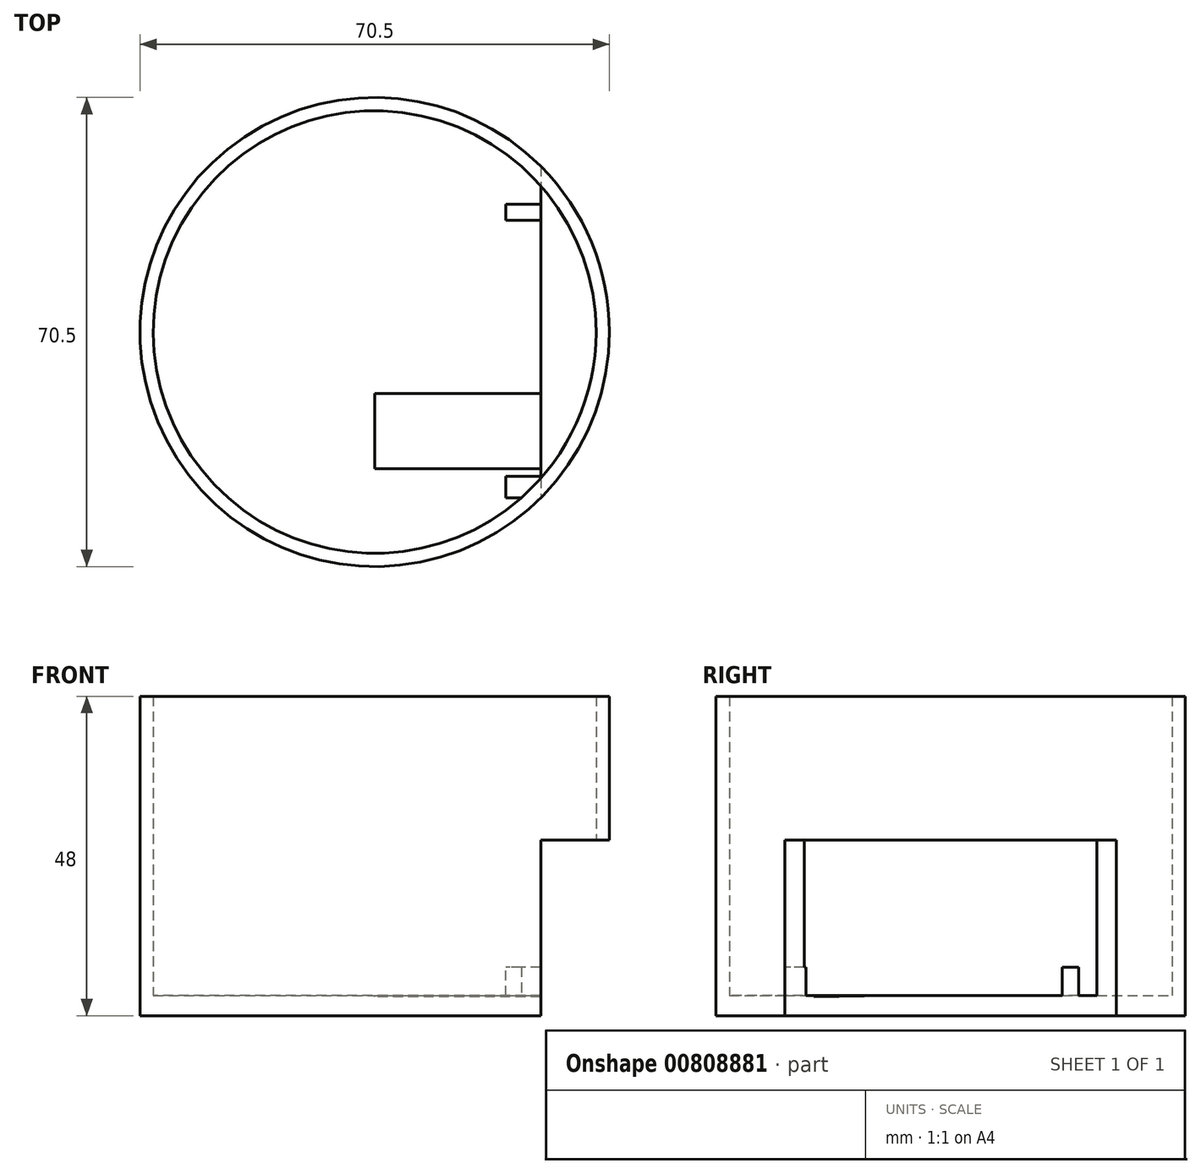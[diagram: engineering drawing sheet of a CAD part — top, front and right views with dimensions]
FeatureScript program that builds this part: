
annotation { "Feature Type Name" : "Feature", "Feature Type Description" : "" }
export const myFeature = defineFeature(function(context is Context, id is Id, definition is map)
    precondition{}
    {
        {
            var Q0;
            Q0=qCreatedBy(makeId("Top.planeOp"),FACE);
            var sketch = newSketch(context, id + "F0", { "sketchPlane" : qUnion([Q0])});
            skCircle(sketch, "E0", {"center": v(0, 0) * mm, "radius": 35.25 * mm});
            skSolve(sketch);
        }
        {
            var Q0;
            Q0=makeQuery(id+"F0.imprint","IMPRINT",FACE,{"disambiguationData":[TD([[makeQuery(id+"F0.imprint","IMPRINT",EDGE,{"derivedFrom":sQuery(id+"F0.wireOp",EDGE,"E0")}),1.0]])]});
            extrude(context, id + "F1", {"entities" : qUnion([Q0]), "depth" : 3 * mm, "offsetDistance" : 25 * mm});
        }
        {
            var Q0;
            Q0=makeQuery(id+"F1.opExtrude","CAP_FACE",FACE,{"disambiguationData":[OSD([sQuery(id+"F0.wireOp",EDGE,"E0")])],"isStart":false});
            var sketch = newSketch(context, id + "F2", { "sketchPlane" : qUnion([Q0])});
            skCircle(sketch, "E1", {"center": v(0, 0) * mm, "radius": 35.25 * mm});
            skCircle(sketch, "E2", {"center": v(0, 0) * mm, "radius": 33.25 * mm});
            skSolve(sketch);
        }
        {
            var Q0;
            Q0=makeQuery(id+"F2.imprint","IMPRINT",FACE,{"disambiguationData":[TD([[makeQuery(id+"F2.imprint","IMPRINT",EDGE,{"derivedFrom":sQuery(id+"F2.wireOp",EDGE,"E1")}),1.0]])]});
            extrude(context, id + "F3", {"entities" : qUnion([Q0]), "operationType" : NewBodyOperationType.ADD, "depth" : 45 * mm, "offsetDistance" : 25 * mm});
        }
        {
            var Q0;
            Q0=qCreatedBy(makeId("Right.planeOp"),FACE);
            var sketch = newSketch(context, id + "F4", { "sketchPlane" : qUnion([Q0])});
            skLineSegment(sketch, "E3.bottom", {"start": v(19.22, 0) * mm, "end": v(-24.9, 0) * mm});
            skLineSegment(sketch, "E3.top", {"start": v(19.22, 26.4) * mm, "end": v(-24.9, 26.4) * mm});
            skLineSegment(sketch, "E3.left", {"start": v(19.22, 0) * mm, "end": v(19.22, 26.4) * mm});
            skLineSegment(sketch, "E3.right", {"start": v(-24.9, 0) * mm, "end": v(-24.9, 26.4) * mm});
            skLineSegment(sketch, "E4.bottom", {"start": v(-21.71, 22.96) * mm, "end": v(16.77, 22.96) * mm});
            skLineSegment(sketch, "E4.top", {"start": v(-21.71, 2.61) * mm, "end": v(16.77, 2.61) * mm});
            skLineSegment(sketch, "E4.left", {"start": v(-21.71, 22.96) * mm, "end": v(-21.71, 2.61) * mm});
            skLineSegment(sketch, "E4.right", {"start": v(16.77, 22.96) * mm, "end": v(16.77, 2.61) * mm});
            skSolve(sketch);
        }
        {
            var Q0;
            Q0=makeQuery(id+"F4.imprint","IMPRINT",FACE,{"disambiguationData":[TD([[makeQuery(id+"F4.imprint","IMPRINT",EDGE,{"derivedFrom":sQuery(id+"F4.wireOp",EDGE,"E3.bottom")}),-1.0]])]});
            extrude(context, id + "F5", {"entities" : qUnion([Q0]), "operationType" : NewBodyOperationType.ADD, "depth" : 54 * mm, "offsetDistance" : 25 * mm, "hasSecondDirection" : true, "secondDirectionOppositeDirection" : false, "secondDirectionDepth" : 19.7 * mm});
        }
        {
            var Q0;
            {var subQ2=sQuery(id+"F4.wireOp",EDGE,"E3.top");Q0=makeQuery(id+"F5.boolean.opBoolean","SPLIT",FACE,{"disambiguationData":[TD([makeQuery(id+"F3.opExtrude","SWEPT_FACE",FACE,{"disambiguationData":[OSD([sQuery(id+"F2.wireOp",EDGE,"E2")])]})])],"derivedFrom":makeQuery(id+"F5.opExtrude","SWEPT_FACE",FACE,{"disambiguationData":[OSD([subQ2])]})});}
            extrude(context, id + "F6", {"entities" : qUnion([Q0]), "operationType" : NewBodyOperationType.REMOVE, "oppositeDirection" : true, "depth" : 19.1 * mm, "offsetDistance" : 25 * mm});
        }
        {
            var Q0;
            Q0=qCreatedBy(makeId("Right.planeOp"),FACE);
            var sketch = newSketch(context, id + "F7", { "sketchPlane" : qUnion([Q0])});
            skLineSegment(sketch, "E5.right", {"start": v(67.36, 28.2) * mm, "end": v(67.36, 30.11) * mm});
            skLineSegment(sketch, "E6.right", {"start": v(15.58, 21.78) * mm, "end": v(15.58, 3.3) * mm});
            skLineSegment(sketch, "E7", {"start": v(-20.55, 21.98) * mm, "end": v(15.58, 21.78) * mm});
            skLineSegment(sketch, "E8", {"start": v(-20.55, 2.86) * mm, "end": v(15.58, 3.3) * mm});
            skLineSegment(sketch, "E9", {"start": v(-20.55, 2.86) * mm, "end": v(-20.55, 21.98) * mm});
            skSolve(sketch);
        }
        {
            var Q0;
            Q0=makeQuery(id+"F7.imprint","IMPRINT",FACE,{"disambiguationData":[TD([[makeQuery(id+"F7.imprint","IMPRINT",EDGE,{"derivedFrom":sQuery(id+"F7.wireOp",EDGE,"E6.right")}),-1.0]])]});
            extrude(context, id + "F8", {"entities" : qUnion([Q0]), "operationType" : NewBodyOperationType.REMOVE, "depth" : 82.1 * mm, "offsetDistance" : 25 * mm});
        }
        {
            var Q0;
            {var subQ1=sQuery(id+"F0.wireOp",EDGE,"E0");var subQ2=sQuery(id+"F4.wireOp",EDGE,"E3.right");Q0=makeQuery(id+"F5.boolean.opBoolean","SPLIT",FACE,{"disambiguationData":[TD([makeQuery(id+"F1.opExtrude","SWEPT_FACE",FACE,{"disambiguationData":[OSD([subQ1])]})])],"derivedFrom":makeQuery(id+"F5.opExtrude","SWEPT_FACE",FACE,{"disambiguationData":[OSD([subQ2])]})});}
            extrude(context, id + "F9", {"entities" : qUnion([Q0]), "operationType" : NewBodyOperationType.REMOVE, "oppositeDirection" : true, "depth" : 75.3 * mm, "offsetDistance" : 25 * mm});
        }
    });
